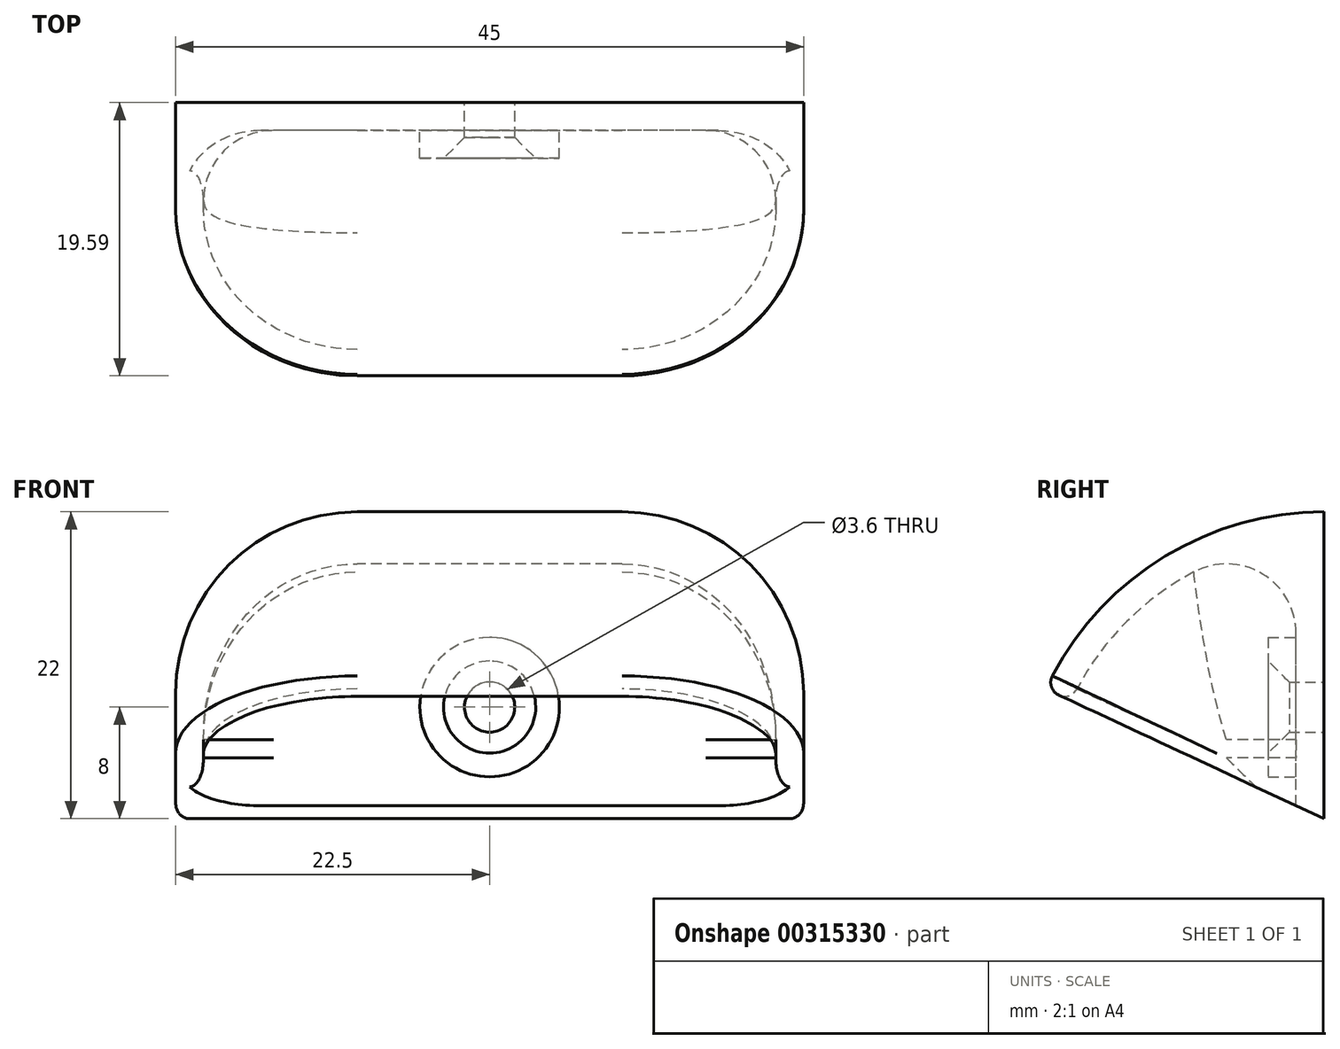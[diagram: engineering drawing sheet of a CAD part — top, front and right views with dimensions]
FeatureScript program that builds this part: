
annotation { "Feature Type Name" : "Feature", "Feature Type Description" : "" }
export const myFeature = defineFeature(function(context is Context, id is Id, definition is map)
    precondition{}
    {
        {
            var Q0;
            Q0=qCreatedBy(makeId("Front.planeOp"),FACE);
            var sketch = newSketch(context, id + "F0", { "sketchPlane" : qUnion([Q0])});
            skLineSegment(sketch, "E0.bottom", {"start": v(22.5, 11) * mm, "end": v(-22.5, 11) * mm});
            skLineSegment(sketch, "E0.top", {"start": v(22.5, -11) * mm, "end": v(-22.5, -11) * mm});
            skLineSegment(sketch, "E0.left", {"start": v(22.5, 11) * mm, "end": v(22.5, -11) * mm});
            skLineSegment(sketch, "E0.right", {"start": v(-22.5, 11) * mm, "end": v(-22.5, -11) * mm});
            skPoint(sketch, "E0.middle", {"position": v(0, 0) * mm});
            skSolve(sketch);
        }
        {
            var Q0;
            Q0=makeQuery(id+"F0.imprint","IMPRINT",FACE,{"disambiguationData":[TD([[makeQuery(id+"F0.imprint","IMPRINT",EDGE,{"derivedFrom":sQuery(id+"F0.wireOp",EDGE,"E0.bottom")}),1.0]])]});
            var Q1;
            Q1=sQuery(id+"F0.wireOp",EDGE,"E0.top");
            revolve(context, id + "F1", {"entities" : qUnion([Q0]), "axis" : qUnion([Q1]), "revolveType" : RevolveType.ONE_DIRECTION, "oppositeDirection" : true, "angle" : 65 * degree});
        }
        {
            var Q0;
            Q0=makeQuery(id+"F1.opRevolve","SWEPT_EDGE",EDGE,{"disambiguationData":[OSD([sQuery(id+"F0.wireOp",EDGE,"E0.bottom"),sQuery(id+"F0.wireOp",EDGE,"E0.left")])]});
            var Q1;
            Q1=makeQuery(id+"F1.opRevolve","SWEPT_EDGE",EDGE,{"disambiguationData":[OSD([sQuery(id+"F0.wireOp",EDGE,"E0.bottom"),sQuery(id+"F0.wireOp",EDGE,"E0.right")])]});
            fillet(context, id + "F2", {"entities" : qUnion([Q0, Q1]), "radius" : 13 * mm, "tangentPropagation" : true, "allowEdgeOverflow" : false});
        }
        {
            var Q0;
            Q0=makeQuery(id+"F1.opRevolve","CAP_FACE",FACE,{"disambiguationData":[OSD([sQuery(id+"F0.wireOp",EDGE,"E0.bottom"),sQuery(id+"F0.wireOp",EDGE,"E0.top"),sQuery(id+"F0.wireOp",EDGE,"E0.left"),sQuery(id+"F0.wireOp",EDGE,"E0.right")])],"isStart":false});
            shell(context, id + "F3", {"entities" : qUnion([Q0]), "thickness" : 2 * mm});
        }
        {
            var Q0;
            Q0=qCreatedBy(makeId("Top.planeOp"),FACE);
            var sketch = newSketch(context, id + "F4", { "sketchPlane" : qUnion([Q0])});
            skLineSegment(sketch, "E1", {"start": v(5, 0) * mm, "end": v(5, -18.13) * mm});
            skLineSegment(sketch, "E2", {"start": v(5, -18.13) * mm, "end": v(-5, -18.13) * mm});
            skLineSegment(sketch, "E3", {"start": v(-5, -18.13) * mm, "end": v(-5, 0) * mm});
            skLineSegment(sketch, "E4", {"start": v(-5, 0) * mm, "end": v(5, 0) * mm});
            skSolve(sketch);
        }
        {
            var Q0;
            Q0=makeQuery(id+"F1.opRevolve","CAP_FACE",FACE,{"disambiguationData":[OSD([sQuery(id+"F0.wireOp",EDGE,"E0.bottom"),sQuery(id+"F0.wireOp",EDGE,"E0.top"),sQuery(id+"F0.wireOp",EDGE,"E0.left"),sQuery(id+"F0.wireOp",EDGE,"E0.right")])],"isStart":true});
            var sketch = newSketch(context, id + "F5", { "sketchPlane" : qUnion([Q0])});
            skCircle(sketch, "E5", {"center": v(0, -3) * mm, "radius": 5 * mm});
            skCircle(sketch, "E6", {"center": v(0, -3) * mm, "radius": 1.8 * mm});
            skSolve(sketch);
        }
        {
            var Q0;
            Q0 = qSketchRegion(id + "F5", true);
            extrude(context, id + "F6", {"entities" : qUnion([Q0]), "operationType" : NewBodyOperationType.ADD, "oppositeDirection" : true, "depth" : 4 * mm});
        }
        {
            var Q0;
            Q0=makeQuery(id+"F6.opExtrude","CAP_EDGE",EDGE,{"disambiguationData":[OSD([sQuery(id+"F5.wireOp",EDGE,"E6")])],"isStart":false});
            chamfer(context, id + "F7", {"entities" : qUnion([Q0]), "width" : 1.5 * mm, "tangentPropagation" : true});
        }
        {
            var Q0;
            Q0=makeQuery(id+"F5.imprint","IMPRINT",FACE,{"disambiguationData":[TD([[makeQuery(id+"F5.imprint","IMPRINT",EDGE,{"derivedFrom":sQuery(id+"F5.wireOp",EDGE,"E6")}),1.0]])]});
            extrude(context, id + "F8", {"entities" : qUnion([Q0]), "operationType" : NewBodyOperationType.REMOVE, "oppositeDirection" : true, "depth" : 10 * mm});
        }
        {
            var Q0;
            {var subQ0=sQuery(id+"F0.wireOp",EDGE,"E0.right");var subQ1=sQuery(id+"F0.wireOp",EDGE,"E0.left");var subQ2=sQuery(id+"F0.wireOp",EDGE,"E0.top");var subQ3=sQuery(id+"F0.wireOp",EDGE,"E0.bottom");Q0=makeQuery(id+"F3.opShell","OFFSET_EDGE",EDGE,{"disambiguationData":[OSD([subQ3,subQ2,subQ1,subQ0]),TDD([makeQuery(id+"F2.opFillet","BLEND_EDGE",EDGE,{"blendedFrom":[makeQuery(id+"F1.opRevolve","SWEPT_EDGE",EDGE,{"disambiguationData":[OSD([subQ3,subQ0])]}),makeQuery(id+"F1.opRevolve","CAP_FACE",FACE,{"disambiguationData":[OSD([subQ3,subQ2,subQ1,subQ0])],"isStart":false})],"blendedInto":[makeQuery(id+"F1.opRevolve","CAP_FACE",FACE,{"disambiguationData":[OSD([subQ3,subQ2,subQ1,subQ0])],"isStart":false})]})])]});}
            fillet(context, id + "F9", {"entities" : qUnion([Q0]), "radius" : 1 * mm, "tangentPropagation" : true, "allowEdgeOverflow" : false});
        }
        {
            var Q0;
            Q0=makeQuery(id+"F1.opRevolve","CAP_EDGE",EDGE,{"disambiguationData":[OSD([sQuery(id+"F0.wireOp",EDGE,"E0.bottom")])],"isStart":false});
            fillet(context, id + "F10", {"entities" : qUnion([Q0]), "radius" : 1 * mm, "tangentPropagation" : true, "allowEdgeOverflow" : false});
        }
        {
            var Q0;
            {var subQ0=sQuery(id+"F0.wireOp",EDGE,"E0.right");var subQ1=sQuery(id+"F0.wireOp",EDGE,"E0.left");var subQ2=sQuery(id+"F0.wireOp",EDGE,"E0.top");var subQ3=sQuery(id+"F0.wireOp",EDGE,"E0.bottom");Q0=makeQuery(id+"F3.opShell","OFFSET_EDGE",EDGE,{"disambiguationData":[OSD([subQ3,subQ2,subQ1,subQ0]),TDD([makeQuery(id+"F2.opFillet","BLEND_EDGE",EDGE,{"blendedFrom":[makeQuery(id+"F1.opRevolve","SWEPT_EDGE",EDGE,{"disambiguationData":[OSD([subQ3,subQ0])]}),makeQuery(id+"F1.opRevolve","CAP_FACE",FACE,{"disambiguationData":[OSD([subQ3,subQ2,subQ1,subQ0])],"isStart":true})],"blendedInto":[makeQuery(id+"F1.opRevolve","CAP_FACE",FACE,{"disambiguationData":[OSD([subQ3,subQ2,subQ1,subQ0])],"isStart":true})]})])]});}
            fillet(context, id + "F11", {"entities" : qUnion([Q0]), "radius" : 5 * mm, "tangentPropagation" : true, "allowEdgeOverflow" : false});
        }
    });
